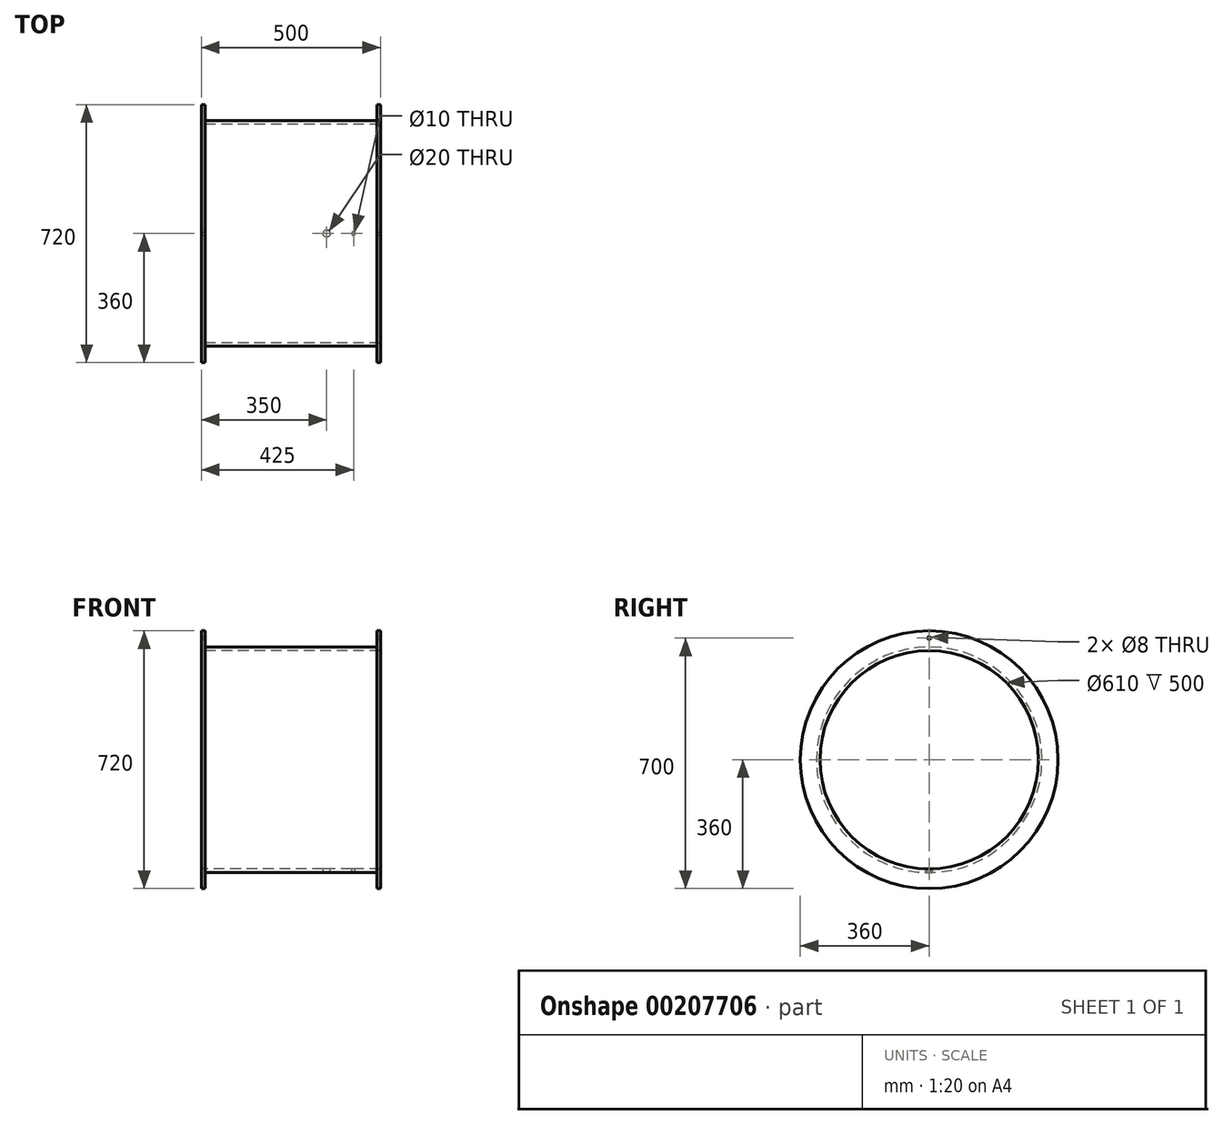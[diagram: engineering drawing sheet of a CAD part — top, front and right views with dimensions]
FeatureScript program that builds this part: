
annotation { "Feature Type Name" : "Feature", "Feature Type Description" : "" }
export const myFeature = defineFeature(function(context is Context, id is Id, definition is map)
    precondition{}
    {
        {
            var Q0;
            Q0=qCreatedBy(makeId("Front.planeOp"),FACE);
            var sketch = newSketch(context, id + "F0", { "sketchPlane" : qUnion([Q0])});
            skLineSegment(sketch, "E0", {"start": v(0, 305) * mm, "end": v(250, 305) * mm});
            skLineSegment(sketch, "E1", {"start": v(250, 360) * mm, "end": v(250, 305) * mm});
            skLineSegment(sketch, "E2.0", {"start": v(240, 360) * mm, "end": v(240, 315) * mm});
            skLineSegment(sketch, "E2.1", {"start": v(0, 315) * mm, "end": v(240, 315) * mm});
            skLineSegment(sketch, "E3", {"start": v(240, 360) * mm, "end": v(250, 360) * mm});
            skLineSegment(sketch, "E4", {"start": v(0, 315) * mm, "end": v(0, 305) * mm, "construction": true});
            skLineSegment(sketch, "E5.MirrorCS", {"start": v(-240, 360) * mm, "end": v(-250, 360) * mm});
            skLineSegment(sketch, "E6.MirrorCS", {"start": v(0, 305) * mm, "end": v(-250, 305) * mm});
            skLineSegment(sketch, "E7.MirrorCS", {"start": v(-240, 360) * mm, "end": v(-240, 315) * mm});
            skLineSegment(sketch, "E8.MirrorCS", {"start": v(-250, 360) * mm, "end": v(-250, 305) * mm});
            skLineSegment(sketch, "E9.MirrorCS", {"start": v(0, 315) * mm, "end": v(-240, 315) * mm});
            skLineSegment(sketch, "E10", {"start": v(0, 0) * mm, "end": v(250, 0) * mm, "construction": true});
            skSolve(sketch);
        }
        {
            var Q0;
            Q0=makeQuery(id+"F0.imprint","IMPRINT",FACE,{"disambiguationData":[TD([[makeQuery(id+"F0.imprint","IMPRINT",EDGE,{"derivedFrom":sQuery(id+"F0.wireOp",EDGE,"E0")}),1.0]])]});
            var Q1;
            Q1=sQuery(id+"F0.wireOp",EDGE,"E10");
            revolve(context, id + "F1", {"entities" : qUnion([Q0]), "axis" : qUnion([Q1]), "revolveType" : RevolveType.FULL});
        }
        {
            var Q0;
            Q0=makeQuery(id+"F1.opRevolve","SWEPT_FACE",FACE,{"disambiguationData":[OSD([sQuery(id+"F0.wireOp",EDGE,"E1")])]});
            var sketch = newSketch(context, id + "F2", { "sketchPlane" : qUnion([Q0])});
            skCircle(sketch, "E11", {"center": v(0, 340) * mm, "radius": 4 * mm});
            skSolve(sketch);
        }
        {
            var Q0;
            Q0=makeQuery(id+"F2.imprint","IMPRINT",FACE,{"disambiguationData":[TD([[makeQuery(id+"F2.imprint","IMPRINT",EDGE,{"derivedFrom":sQuery(id+"F2.wireOp",EDGE,"E11")}),1.0]])]});
            extrude(context, id + "F3", {"entities" : qUnion([Q0]), "operationType" : NewBodyOperationType.REMOVE, "endBound" : BoundingType.THROUGH_ALL, "oppositeDirection" : true, "depth" : 25 * mm});
        }
        {
            var Q0;
            Q0=qCreatedBy(makeId("Top.planeOp"),FACE);
            var sketch = newSketch(context, id + "F4", { "sketchPlane" : qUnion([Q0])});
            skCircle(sketch, "E12", {"center": v(100, 0) * mm, "radius": 10 * mm});
            skCircle(sketch, "E13", {"center": v(175, 0) * mm, "radius": 5 * mm});
            skSolve(sketch);
        }
        {
            var Q0;
            Q0 = qSketchRegion(id + "F4", true);
            extrude(context, id + "F5", {"entities" : qUnion([Q0]), "operationType" : NewBodyOperationType.REMOVE, "endBound" : BoundingType.THROUGH_ALL, "oppositeDirection" : true, "depth" : 25 * mm});
        }
    });
